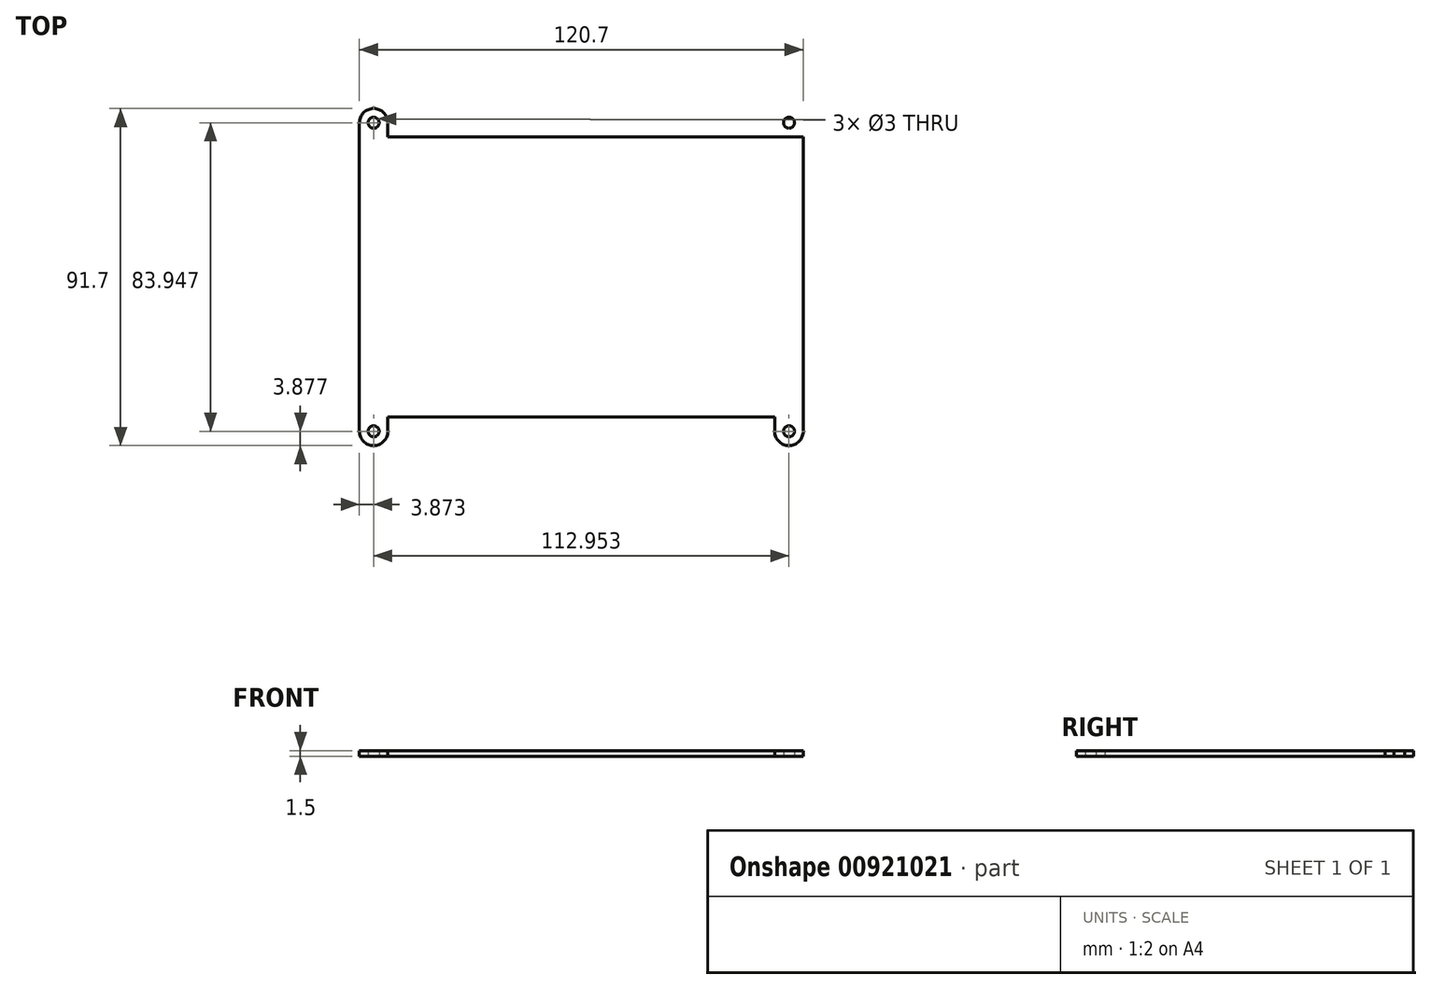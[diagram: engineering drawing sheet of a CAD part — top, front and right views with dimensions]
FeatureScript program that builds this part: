
annotation { "Feature Type Name" : "Feature", "Feature Type Description" : "" }
export const myFeature = defineFeature(function(context is Context, id is Id, definition is map)
    precondition{}
    {
        {
            var Q0;
            Q0=qCreatedBy(makeId("Top.planeOp"),FACE);
            var sketch = newSketch(context, id + "F0", { "sketchPlane" : qUnion([Q0])});
            skLineSegment(sketch, "E0.bottom", {"start": v(-60.35, 38.1) * mm, "end": v(60.35, 38.1) * mm});
            skLineSegment(sketch, "E0.top", {"start": v(-60.35, -38.1) * mm, "end": v(60.35, -38.1) * mm});
            skLineSegment(sketch, "E0.left", {"start": v(-60.35, 38.1) * mm, "end": v(-60.35, -38.1) * mm});
            skLineSegment(sketch, "E0.right", {"start": v(60.35, 38.1) * mm, "end": v(60.35, -38.1) * mm});
            skLineSegment(sketch, "E1", {"start": v(0, 38.1) * mm, "end": v(0, -38.1) * mm, "construction": true});
            skLineSegment(sketch, "E2", {"start": v(-60.35, 0) * mm, "end": v(60.35, 0) * mm, "construction": true});
            skLineSegment(sketch, "E3.left", {"start": v(-60.35, 38.1) * mm, "end": v(-60.35, 41.97) * mm});
            skLineSegment(sketch, "E3.right", {"start": v(-52.6, 38.1) * mm, "end": v(-52.6, 41.97) * mm});
            skPoint(sketch, "E4", {"position": v(-60.35, 41.97) * mm});
            skPoint(sketch, "E5", {"position": v(-52.6, 41.97) * mm});
            skArc(sketch, "E6", {"start": v(-52.6, 41.97) * mm, "mid": v(-56.48, 45.85) * mm, "end": v(-60.35, 41.97) * mm});
            skCircle(sketch, "E7", {"center": v(-56.48, 41.97) * mm, "radius": 1.5 * mm});
            skCircle(sketch, "E8.MirrorC", {"center": v(56.48, 41.97) * mm, "radius": 1.5 * mm});
            skLineSegment(sketch, "E9.MirrorCS", {"start": v(52.6, 38.1) * mm, "end": v(52.6, 41.97) * mm});
            skArc(sketch, "E10.MirrorCS", {"start": v(52.6, 41.97) * mm, "mid": v(56.48, 45.85) * mm, "end": v(60.35, 41.97) * mm});
            skLineSegment(sketch, "E11.MirrorCS", {"start": v(60.35, 38.1) * mm, "end": v(60.35, 41.97) * mm});
            skCircle(sketch, "E12.MirrorC", {"center": v(56.48, -41.97) * mm, "radius": 1.5 * mm});
            skLineSegment(sketch, "E13.MirrorCS", {"start": v(52.6, -38.1) * mm, "end": v(52.6, -41.97) * mm});
            skArc(sketch, "E14.MirrorCS", {"start": v(52.6, -41.97) * mm, "mid": v(56.48, -45.85) * mm, "end": v(60.35, -41.97) * mm});
            skLineSegment(sketch, "E15.MirrorCS", {"start": v(60.35, -38.1) * mm, "end": v(60.35, -41.97) * mm});
            skLineSegment(sketch, "E16.MirrorCS", {"start": v(-60.35, -38.1) * mm, "end": v(-60.35, -41.97) * mm});
            skCircle(sketch, "E17.MirrorC", {"center": v(-56.48, -41.97) * mm, "radius": 1.5 * mm});
            skLineSegment(sketch, "E18.MirrorCS", {"start": v(-52.6, -38.1) * mm, "end": v(-52.6, -41.97) * mm});
            skArc(sketch, "E19.MirrorCS", {"start": v(-52.6, -41.97) * mm, "mid": v(-56.48, -45.85) * mm, "end": v(-60.35, -41.97) * mm});
            skPoint(sketch, "E20", {"position": v(-60.35, 38.1) * mm});
            skSolve(sketch);
        }
        {
            var Q0;
            {var subQ1=sQuery(id+"F0.wireOp",EDGE,"E16.MirrorCS");Q0=makeQuery(id+"F0.imprint","IMPRINT",FACE,{"disambiguationData":[TD([[makeQuery(id+"F0.imprint","IMPRINT",EDGE,{"derivedFrom":subQ1}),1.0]])]});}
            var Q1;
            Q1=makeQuery(id+"F0.imprint","IMPRINT",FACE,{"disambiguationData":[TD([[makeQuery(id+"F0.imprint","IMPRINT",EDGE,{"derivedFrom":sQuery(id+"F0.wireOp",EDGE,"E8.MirrorC")}),1.0]])]});
            var Q2;
            {var subQ0=sQuery(id+"F0.wireOp",EDGE,"E0.left");Q2=makeQuery(id+"F0.imprint","IMPRINT",FACE,{"disambiguationData":[TD([[makeQuery(id+"F0.imprint","IMPRINT",EDGE,{"derivedFrom":subQ0}),1.0]])]});}
            var Q3;
            Q3=makeQuery(id+"F0.imprint","IMPRINT",FACE,{"disambiguationData":[TD([[makeQuery(id+"F0.imprint","IMPRINT",EDGE,{"derivedFrom":sQuery(id+"F0.wireOp",EDGE,"E12.MirrorC")}),-1.0]])]});
            extrude(context, id + "F1", {"entities" : qUnion([Q0, Q1, Q2, Q3]), "depth" : 1.5 * mm, "offsetDistance" : 25.4 * mm});
        }
        {
            var Q0;
            {var subQ1=sQuery(id+"F0.wireOp",EDGE,"E3.left");Q0=makeQuery(id+"F0.imprint","IMPRINT",FACE,{"disambiguationData":[TD([[makeQuery(id+"F0.imprint","IMPRINT",EDGE,{"derivedFrom":subQ1}),-1.0]])]});}
            extrude(context, id + "F2", {"entities" : qUnion([Q0]), "operationType" : NewBodyOperationType.ADD, "depth" : 1.5 * mm, "offsetDistance" : 25 * mm});
        }
    });
